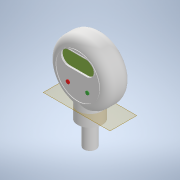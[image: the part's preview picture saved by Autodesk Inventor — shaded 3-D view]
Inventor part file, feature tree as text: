
AUTODESK INVENTOR PART (.ipt)
format: ipt  version: 2021 (Build 250183000, 183)  size: 250,880 bytes
history: native  units: mm
features: extrude x5, sketch x5, other x2, projected_geometry x2, fillet x1
ambient origin geometry x8: Origin, YZ Plane, XZ Plane, XY Plane, X Axis, Y Axis, Z Axis, Center Point
bodies: Body1 (feature_tree)
feature tree (15):
  other  "Bryła1"
  extrude  "Wyciągnięcie proste1"  Depth=50.0mm
  fillet  "Zaokrąglenie1"  Radius=20.0mm
  other  "Płaszczyzna konstrukcyjna1"
  extrude  "Wyciągnięcie proste2"  Depth=7.0mm
  extrude  "Wyciągnięcie proste3"  Depth=10.0mm TaperAngle=0.0deg
  extrude  "Wyciągnięcie proste4"  Depth=10.0mm TaperAngle=0.0deg
  extrude  "Wyciągnięcie proste5"  Depth=10.0mm
  sketch  "Szkic1"
  sketch  "Szkic2"
  sketch  "Szkic3"
  sketch  "Szkic4"
  sketch  "Szkic5"
  projected_geometry  "Pętla rzutowana1"
  projected_geometry  "Pętla rzutowana2"
